# Revit family: TESK_Насос вертикальный_TK32-150
name_source: partatom
category: Оборудование
units: mm (PartAtom-declared; Revit-internal decimal feet)

## family parameters
Всегда вертикально = Да
Классификация = Насос
На основе рабочей плоскости = Нет
Общий = Нет
При загрузке вырезать с полостями = Нет
Размер круглого соединителя = Использовать диаметр
Тип детали = Вставляется
Точка расчета площади = Нет

## types (85) — shared parameters
ADSK_URL документации изделия = https://teskpump.ru
ADSK_Единица измерения = шт.
ADSK_Завод-изготовитель = TESK
ADSK_Классификация нагрузок = Прочее
ADSK_Количество = 1
ADSK_Коэффициент мощности = 1
URL = https://teskpump.ru
Изготовитель = TESK
Материал_1 = TESK_Черный_Условный
Материал_2 = TESK_Черный_Ребра_Условный
Плита_Толщина = 35 мм
Энергоэффективность = IE3

## per-type parameters (varying)
- ТК 32-18/2  1,1kW 3x380V 50Hz IE3: ADSK_Диаметр условный=32 мм; ADSK_Код изделия=55TK3218203380; ADSK_Количество фаз=3; ADSK_Количество фаз числовое=3; ADSK_Марка=ТК 32-18/2  1,1kW 3x380V 50Hz IE3; ADSK_Масса=36; ADSK_Масса_Текст=36; ADSK_Наименование=Вертикальный насос TESK типа IN-LINE, DN32, Hmax=18м (3x380V 50Hz IE3); ADSK_Напряжение=400 В; ADSK_Номинальная мощность=1.10 кВт; ADSK_Полная мощность=1.10 кВ·А; B1=170 мм; B2=142 мм; B3=125 мм; B4=117 мм; B5=144 мм; C=39 мм; D=120 мм; D2=80 мм; D3=134 мм; DN=32 мм; F0=140 мм; F1=78 мм; F2=39 мм; F3=88 мм; F4=104 мм; H1=100 мм; H2=189 мм; H3=540 мм; H4=251 мм; L1=340 мм; Напор максимальный=18; Плита_Глубина=188 мм; Плита_Ширина=188 мм
- ТК 32-21/2  1,5kW 3x380V 50Hz IE3: ADSK_Диаметр условный=32 мм; ADSK_Код изделия=55TK3221203380; ADSK_Количество фаз=3; ADSK_Количество фаз числовое=3; ADSK_Марка=ТК 32-21/2  1,5kW 3x380V 50Hz IE3; ADSK_Масса=40; ADSK_Масса_Текст=40; ADSK_Наименование=Вертикальный насос TESK типа IN-LINE, DN32, Hmax=21м (3x380V 50Hz IE3); ADSK_Напряжение=400 В; ADSK_Номинальная мощность=1.50 кВт; ADSK_Полная мощность=1.50 кВ·А; B1=190 мм; B2=155 мм; B3=125 мм; B4=117 мм; B5=144 мм; C=39 мм; D=140 мм; D2=100 мм; D3=134 мм; DN=32 мм; F0=140 мм; F1=78 мм; F2=39 мм; F3=88 мм; F4=104 мм; H1=100 мм; H2=199 мм; H3=592 мм; H4=293 мм; L1=340 мм; Напор максимальный=21; Плита_Глубина=188 мм; Плита_Ширина=188 мм
- ТК 32-25/2  2,2kW 3x380V 50Hz IE3: ADSK_Диаметр условный=32 мм; ADSK_Код изделия=55TK3225203380; ADSK_Количество фаз=3; ADSK_Количество фаз числовое=3; ADSK_Марка=ТК 32-25/2  2,2kW 3x380V 50Hz IE3; ADSK_Масса=42; ADSK_Масса_Текст=42; ADSK_Наименование=Вертикальный насос TESK типа IN-LINE, DN32, Hmax=25м (3x380V 50Hz IE3); ADSK_Напряжение=400 В; ADSK_Номинальная мощность=2.20 кВт; ADSK_Полная мощность=2.20 кВ·А; B1=190 мм; B2=155 мм; B3=125 мм; B4=117 мм; B5=144 мм; C=39 мм; D=140 мм; D2=100 мм; D3=134 мм; DN=32 мм; F0=140 мм; F1=78 мм; F2=39 мм; F3=88 мм; F4=104 мм; H1=100 мм; H2=199 мм; H3=592 мм; H4=293 мм; L1=340 мм; Напор максимальный=25; Плита_Глубина=188 мм; Плита_Ширина=188 мм
- ТК 32-18/2  1,1kW 1x220V 50Hz IE3: ADSK_Диаметр условный=32 мм; ADSK_Код изделия=55TK3218201220; ADSK_Количество фаз=1; ADSK_Количество фаз числовое=1; ADSK_Марка=ТК32-18/2  1,1kW 1x220V 50Hz IE3; ADSK_Масса=36; ADSK_Масса_Текст=36; ADSK_Наименование=Вертикальный насос TESK типа IN-LINE, DN32, Hmax=18м (1x220V 50Hz IE3); ADSK_Напряжение=230 В; ADSK_Номинальная мощность=1.10 кВт; ADSK_Полная мощность=1.10 кВ·А; B1=170 мм; B2=142 мм; B3=125 мм; B4=117 мм; B5=144 мм; C=39 мм; D=120 мм; D2=80 мм; D3=134 мм; DN=32 мм; F0=140 мм; F1=78 мм; F2=39 мм; F3=88 мм; F4=104 мм; H1=100 мм; H2=189 мм; H3=540 мм; H4=251 мм; L1=340 мм; Напор максимальный=18; Плита_Глубина=188 мм; Плита_Ширина=188 мм
- ТК 32-21/2  1,5kW 1x220V 50Hz IE3: ADSK_Диаметр условный=32 мм; ADSK_Код изделия=55TK3221201220; ADSK_Количество фаз=1; ADSK_Количество фаз числовое=1; ADSK_Марка=ТК32-21/2  1,5kW 1x220V 50Hz IE3; ADSK_Масса=40; ADSK_Масса_Текст=40; ADSK_Наименование=Вертикальный насос TESK типа IN-LINE, DN32, Hmax=21м (1x220V 50Hz IE3); ADSK_Напряжение=230 В; ADSK_Номинальная мощность=1.50 кВт; ADSK_Полная мощность=1.50 кВ·А; B1=190 мм; B2=155 мм; B3=125 мм; B4=117 мм; B5=144 мм; C=39 мм; D=140 мм; D2=100 мм; D3=134 мм; DN=32 мм; F0=140 мм; F1=78 мм; F2=39 мм; F3=88 мм; F4=104 мм; H1=100 мм; H2=199 мм; H3=592 мм; H4=293 мм; L1=340 мм; Напор максимальный=21; Плита_Глубина=188 мм; Плита_Ширина=188 мм
- ТК 32-25/2  2,2kW 1x220V 50Hz IE3: ADSK_Диаметр условный=32 мм; ADSK_Код изделия=55TK3225201220; ADSK_Количество фаз=1; ADSK_Количество фаз числовое=1; ADSK_Марка=ТК32-25/2  2,2kW 1x220V 50Hz IE3; ADSK_Масса=42; ADSK_Масса_Текст=42; ADSK_Наименование=Вертикальный насос TESK типа IN-LINE, DN32, Hmax=25м (1x220V 50Hz IE3); ADSK_Напряжение=230 В; ADSK_Номинальная мощность=2.20 кВт; ADSK_Полная мощность=2.20 кВ·А; B1=190 мм; B2=155 мм; B3=125 мм; B4=117 мм; B5=144 мм; C=39 мм; D=140 мм; D2=100 мм; D3=134 мм; DN=32 мм; F0=140 мм; F1=78 мм; F2=39 мм; F3=88 мм; F4=104 мм; H1=100 мм; H2=199 мм; H3=592 мм; H4=293 мм; L1=340 мм; Напор максимальный=25; Плита_Глубина=188 мм; Плита_Ширина=188 мм
- ТК 32-32/2  3kW 3x380V 50Hz IE3: ADSK_Диаметр условный=32 мм; ADSK_Код изделия=55TK3232203380; ADSK_Количество фаз=3; ADSK_Количество фаз числовое=3; ADSK_Марка=ТК 32-32/2  3kW 3x380V 50Hz IE3; ADSK_Масса=48; ADSK_Масса_Текст=48; ADSK_Наименование=Вертикальный насос TESK типа IN-LINE, DN32, Hmax=32м (3x380V 50Hz IE3); ADSK_Напряжение=400 В; ADSK_Номинальная мощность=3.00 кВт; ADSK_Полная мощность=3.00 кВ·А; B1=197 мм; B2=165 мм; B3=125 мм; B4=117 мм; B5=144 мм; C=39 мм; D=160 мм; D2=120 мм; D3=134 мм; DN=32 мм; F0=140 мм; F1=78 мм; F2=39 мм; F3=88 мм; F4=104 мм; H1=100 мм; H2=205 мм; H3=619 мм; H4=314 мм; L1=340 мм; Напор максимальный=32; Плита_Глубина=188 мм; Плита_Ширина=188 мм
- ТК 32-38/2  4kW 3x380V 50Hz IE3: ADSK_Диаметр условный=32 мм; ADSK_Код изделия=55TK3238203380; ADSK_Количество фаз=3; ADSK_Количество фаз числовое=3; ADSK_Марка=ТК 32-38/2  4kW 3x380V 50Hz IE3; ADSK_Масса=64; ADSK_Масса_Текст=64; ADSK_Наименование=Вертикальный насос TESK типа IN-LINE, DN32, Hmax=38м (3x380V 50Hz IE3); ADSK_Напряжение=400 В; ADSK_Номинальная мощность=4.00 кВт; ADSK_Полная мощность=4.00 кВ·А; B1=230 мм; B2=188 мм; B3=144 мм; B4=144 мм; B5=144 мм; C=39 мм; D=160 мм; D2=120 мм; D3=188 мм; DN=32 мм; F0=140 мм; F1=78 мм; F2=39 мм; F3=88 мм; F4=104 мм; H1=100 мм; H2=207 мм; H3=642 мм; H4=335 мм; L1=440 мм; Напор максимальный=38; Плита_Глубина=188 мм; Плита_Ширина=188 мм
- ТК 32-50/2  5,5kW 3x380V 50Hz IE3: ADSK_Диаметр условный=32 мм; ADSK_Код изделия=55TK3250203380; ADSK_Количество фаз=3; ADSK_Количество фаз числовое=3; ADSK_Марка=ТК 32-50/2  5,5kW 3x380V 50Hz IE3; ADSK_Масса=85; ADSK_Масса_Текст=85; ADSK_Наименование=Вертикальный насос TESK типа IN-LINE, DN32, Hmax=50м (3x380V 50Hz IE3); ADSK_Напряжение=400 В; ADSK_Номинальная мощность=5.50 кВт; ADSK_Полная мощность=5.50 кВ·А; B1=260 мм; B2=208 мм; B3=144 мм; B4=144 мм; B5=144 мм; C=39 мм; D=200 мм; D2=160 мм; D3=188 мм; DN=32 мм; F0=140 мм; F1=78 мм; F2=39 мм; F3=88 мм; F4=104 мм; H1=100 мм; H2=227 мм; H3=737 мм; H4=410 мм; L1=440 мм; Напор максимальный=50; Плита_Глубина=188 мм; Плита_Ширина=188 мм
- ТК 40-16/2  1,1kW 3x380V 50Hz IE3: ADSK_Диаметр условный=40 мм; ADSK_Код изделия=55TK4016203380; ADSK_Количество фаз=3; ADSK_Количество фаз числовое=3; ADSK_Марка=ТК 40-16/2  1,1kW 3x380V 50Hz IE3; ADSK_Масса=31; ADSK_Масса_Текст=31; ADSK_Наименование=Вертикальный насос TESK типа IN-LINE, DN40, Hmax=16м (3x380V 50Hz IE3); ADSK_Напряжение=400 В; ADSK_Номинальная мощность=1.10 кВт; ADSK_Полная мощность=1.10 кВ·А; B1=170 мм; B2=142 мм; B3=97 мм; B4=96 мм; B5=120 мм; C=44 мм; D=120 мм; D2=80 мм; D3=92 мм; DN=40 мм; F0=150 мм; F1=88 мм; F2=44 мм; F3=94 мм; F4=111 мм; H1=68 мм; H2=178 мм; H3=497 мм; H4=251 мм; L1=320 мм; Напор максимальный=16; Плита_Глубина=164 мм; Плита_Ширина=164 мм
- ТК 40-18/2  1,5kW 3x380V 50Hz IE3: ADSK_Диаметр условный=40 мм; ADSK_Код изделия=55TK4020203380; ADSK_Количество фаз=3; ADSK_Количество фаз числовое=3; ADSK_Марка=ТК 40-18/2  1,5kW 3x380V 50Hz IE3; ADSK_Масса=36; ADSK_Масса_Текст=36; ADSK_Наименование=Вертикальный насос TESK типа IN-LINE, DN40, Hmax=20м (3x380V 50Hz IE3); ADSK_Напряжение=400 В; ADSK_Номинальная мощность=1.50 кВт; ADSK_Полная мощность=1.50 кВ·А; B1=190 мм; B2=155 мм; B3=97 мм; B4=96 мм; B5=120 мм; C=44 мм; D=140 мм; D2=100 мм; D3=92 мм; DN=40 мм; F0=150 мм; F1=88 мм; F2=44 мм; F3=94 мм; F4=111 мм; H1=68 мм; H2=188 мм; H3=549 мм; H4=293 мм; L1=320 мм; Напор максимальный=20; Плита_Глубина=164 мм; Плита_Ширина=164 мм
- ТК 40-20/2  2,2kW 3x380V 50Hz IE3: ADSK_Диаметр условный=40 мм; ADSK_Код изделия=55TK4018203380; ADSK_Количество фаз=3; ADSK_Количество фаз числовое=3; ADSK_Марка=ТК 40-20/2  2,2kW 3x380V 50Hz IE3; ADSK_Масса=40; ADSK_Масса_Текст=40; ADSK_Наименование=Вертикальный насос TESK типа IN-LINE, DN40, Hmax=18м (3x380V 50Hz IE3); ADSK_Напряжение=400 В; ADSK_Номинальная мощность=2.20 кВт; ADSK_Полная мощность=2.20 кВ·А; B1=190 мм; B2=155 мм; B3=110 мм; B4=95 мм; B5=144 мм; C=44 мм; D=140 мм; D2=100 мм; D3=90 мм; DN=40 мм; F0=150 мм; F1=88 мм; F2=44 мм; F3=94 мм; F4=111 мм; H1=100 мм; H2=195 мм; H3=588 мм; H4=293 мм; L1=340 мм; Напор максимальный=18; Плита_Глубина=188 мм; Плита_Ширина=188 мм
- ТК 40-16/2  1,1kW 1x220V 50Hz IE3: ADSK_Диаметр условный=40 мм; ADSK_Код изделия=55TK4016201220; ADSK_Количество фаз=1; ADSK_Количество фаз числовое=1; ADSK_Марка=ТК 40-16/2  1,1kW 1x220V 50Hz IE3; ADSK_Масса=31; ADSK_Масса_Текст=31; ADSK_Наименование=Вертикальный насос TESK типа IN-LINE, DN40, Hmax=16м (1x220V 50Hz IE3); ADSK_Напряжение=230 В; ADSK_Номинальная мощность=1.10 кВт; ADSK_Полная мощность=1.10 кВ·А; B1=170 мм; B2=142 мм; B3=97 мм; B4=96 мм; B5=120 мм; C=44 мм; D=120 мм; D2=80 мм; D3=92 мм; DN=40 мм; F0=150 мм; F1=88 мм; F2=44 мм; F3=94 мм; F4=111 мм; H1=68 мм; H2=178 мм; H3=497 мм; H4=251 мм; L1=320 мм; Напор максимальный=16; Плита_Глубина=164 мм; Плита_Ширина=164 мм
- ТК 40-20/2  1,5kW 1x220V 50Hz IE3: ADSK_Диаметр условный=40 мм; ADSK_Код изделия=55TK4020201220; ADSK_Количество фаз=1; ADSK_Количество фаз числовое=1; ADSK_Марка=ТК 40-20/2  1,5kW 1x220V 50Hz IE3; ADSK_Масса=36; ADSK_Масса_Текст=36; ADSK_Наименование=Вертикальный насос TESK типа IN-LINE, DN40, Hmax=20м (1x220V 50Hz IE3); ADSK_Напряжение=230 В; ADSK_Номинальная мощность=1.50 кВт; ADSK_Полная мощность=1.50 кВ·А; B1=190 мм; B2=155 мм; B3=97 мм; B4=96 мм; B5=120 мм; C=44 мм; D=140 мм; D2=100 мм; D3=92 мм; DN=40 мм; F0=150 мм; F1=88 мм; F2=44 мм; F3=94 мм; F4=111 мм; H1=68 мм; H2=188 мм; H3=549 мм; H4=293 мм; L1=320 мм; Напор максимальный=20; Плита_Глубина=164 мм; Плита_Ширина=164 мм
- ТК 40-18/2  2,2kW 1x220V 50Hz IE3: ADSK_Диаметр условный=40 мм; ADSK_Код изделия=55TK4018201220; ADSK_Количество фаз=1; ADSK_Количество фаз числовое=1; ADSK_Марка=ТК 40-18/2  2,2kW 1x220V 50Hz IE3; ADSK_Масса=40; ADSK_Масса_Текст=40; ADSK_Наименование=Вертикальный насос TESK типа IN-LINE, DN40, Hmax=18м (1x220V 50Hz IE3); ADSK_Напряжение=230 В; ADSK_Номинальная мощность=2.20 кВт; ADSK_Полная мощность=2.20 кВ·А; B1=190 мм; B2=155 мм; B3=110 мм; B4=95 мм; B5=144 мм; C=44 мм; D=140 мм; D2=100 мм; D3=90 мм; DN=40 мм; F0=150 мм; F1=88 мм; F2=44 мм; F3=94 мм; F4=111 мм; H1=100 мм; H2=195 мм; H3=588 мм; H4=293 мм; L1=340 мм; Напор максимальный=18; Плита_Глубина=188 мм; Плита_Ширина=188 мм
- ТК 40-25/2  3kW 3x380V 50Hz IE3: ADSK_Диаметр условный=40 мм; ADSK_Код изделия=55TK4025203380; ADSK_Количество фаз=3; ADSK_Количество фаз числовое=3; ADSK_Марка=ТК 40-25/2  3kW 3x380V 50Hz IE3; ADSK_Масса=52; ADSK_Масса_Текст=52; ADSK_Наименование=Вертикальный насос TESK типа IN-LINE, DN40, Hmax=25м (3x380V 50Hz IE3); ADSK_Напряжение=400 В; ADSK_Номинальная мощность=3.00 кВт; ADSK_Полная мощность=3.00 кВ·А; B1=197 мм; B2=165 мм; B3=127 мм; B4=115 мм; B5=144 мм; C=44 мм; D=160 мм; D2=120 мм; D3=130 мм; DN=40 мм; F0=150 мм; F1=88 мм; F2=44 мм; F3=94 мм; F4=111 мм; H1=100 мм; H2=207 мм; H3=621 мм; H4=314 мм; L1=340 мм; Напор максимальный=25; Плита_Глубина=188 мм; Плита_Ширина=188 мм
- ТК 40-30/2  4kW 3x380V 50Hz IE3: ADSK_Диаметр условный=40 мм; ADSK_Код изделия=55TK4030203380; ADSK_Количество фаз=3; ADSK_Количество фаз числовое=3; ADSK_Марка=ТК 40-30/2  4kW 3x380V 50Hz IE3; ADSK_Масса=62; ADSK_Масса_Текст=62; ADSK_Наименование=Вертикальный насос TESK типа IN-LINE, DN40, Hmax=30м (3x380V 50Hz IE3); ADSK_Напряжение=400 В; ADSK_Номинальная мощность=4.00 кВт; ADSK_Полная мощность=4.00 кВ·А; B1=230 мм; B2=188 мм; B3=127 мм; B4=115 мм; B5=144 мм; C=44 мм; D=160 мм; D2=120 мм; D3=130 мм; DN=40 мм; F0=150 мм; F1=88 мм; F2=44 мм; F3=94 мм; F4=111 мм; H1=100 мм; H2=207 мм; H3=642 мм; H4=335 мм; L1=340 мм; Напор максимальный=30; Плита_Глубина=188 мм; Плита_Ширина=188 мм
- ТК 40-36/2  5,5kW 3x380V 50Hz IE3: ADSK_Диаметр условный=40 мм; ADSK_Код изделия=55TK4036203380; ADSK_Количество фаз=3; ADSK_Количество фаз числовое=3; ADSK_Марка=ТК 40-36/2  5,5kW 3x380V 50Hz IE3; ADSK_Масса=86; ADSK_Масса_Текст=86; ADSK_Наименование=Вертикальный насос TESK типа IN-LINE, DN40, Hmax=36м (3x380V 50Hz IE3); ADSK_Напряжение=400 В; ADSK_Номинальная мощность=5.50 кВт; ADSK_Полная мощность=5.50 кВ·А; B1=260 мм; B2=208 мм; B3=138 мм; B4=125 мм; B5=144 мм; C=44 мм; D=200 мм; D2=160 мм; D3=150 мм; DN=40 мм; F0=150 мм; F1=88 мм; F2=44 мм; F3=94 мм; F4=111 мм; H1=110 мм; H2=227 мм; H3=747 мм; H4=410 мм; L1=440 мм; Напор максимальный=36; Плита_Глубина=188 мм; Плита_Ширина=188 мм
- ТК 40-48/2  7,5kW 3x380V 50Hz IE3: ADSK_Диаметр условный=40 мм; ADSK_Код изделия=55TK4048203380; ADSK_Количество фаз=3; ADSK_Количество фаз числовое=3; ADSK_Марка=ТК 40-48/2  7,5kW 3x380V 50Hz IE3; ADSK_Масса=95; ADSK_Масса_Текст=95; ADSK_Наименование=Вертикальный насос TESK типа IN-LINE, DN40, Hmax=48м (3x380V 50Hz IE3); ADSK_Напряжение=400 В; ADSK_Номинальная мощность=7.50 кВт; ADSK_Полная мощность=7.50 кВ·А; B1=260 мм; B2=208 мм; B3=138 мм; B4=125 мм; B5=144 мм; C=44 мм; D=200 мм; D2=160 мм; D3=150 мм; DN=40 мм; F0=150 мм; F1=88 мм; F2=44 мм; F3=94 мм; F4=111 мм; H1=110 мм; H2=227 мм; H3=747 мм; H4=410 мм; L1=440 мм; Напор максимальный=48; Плита_Глубина=188 мм; Плита_Ширина=188 мм
- ТК 50-32/2  3kW 3x380V 50Hz IE3: ADSK_Диаметр условный=50 мм; ADSK_Код изделия=55TK5032203380; ADSK_Количество фаз=3; ADSK_Количество фаз числовое=3; ADSK_Марка=ТК 50-32/2  3kW 3x380V 50Hz IE3; ADSK_Масса=58; ADSK_Масса_Текст=58; ADSK_Наименование=Вертикальный насос TESK типа IN-LINE, DN50, Hmax=32м (3x380V 50Hz IE3); ADSK_Напряжение=400 В; ADSK_Номинальная мощность=3.00 кВт; ADSK_Полная мощность=3.00 кВ·А; B1=197 мм; B2=165 мм; B3=128 мм; B4=128 мм; B5=144 мм; C=51 мм; D=160 мм; D2=120 мм; D3=156 мм; DN=50 мм; F0=165 мм; F1=102 мм; F2=51 мм; F3=103 мм; F4=122 мм; H1=105 мм; H2=181 мм; H3=600 мм; H4=314 мм; L1=400 мм; Напор максимальный=32; Плита_Глубина=188 мм; Плита_Ширина=188 мм
- ТК 50-38/2  4kW 3x380V 50Hz IE3: ADSK_Диаметр условный=50 мм; ADSK_Код изделия=55TK5038203380; ADSK_Количество фаз=3; ADSK_Количество фаз числовое=3; ADSK_Марка=ТК 50-38/2  4kW 3x380V 50Hz IE3; ADSK_Масса=68; ADSK_Масса_Текст=68; ADSK_Наименование=Вертикальный насос TESK типа IN-LINE, DN50, Hmax=38м (3x380V 50Hz IE3); ADSK_Напряжение=400 В; ADSK_Номинальная мощность=4.00 кВт; ADSK_Полная мощность=4.00 кВ·А; B1=230 мм; B2=188 мм; B3=128 мм; B4=128 мм; B5=144 мм; C=51 мм; D=160 мм; D2=120 мм; D3=156 мм; DN=50 мм; F0=165 мм; F1=102 мм; F2=51 мм; F3=103 мм; F4=122 мм; H1=105 мм; H2=181 мм; H3=621 мм; H4=335 мм; L1=400 мм; Напор максимальный=38; Плита_Глубина=188 мм; Плита_Ширина=188 мм
- ТК 50-48/2  5,5kW 3x380V 50Hz IE3: ADSK_Диаметр условный=50 мм; ADSK_Код изделия=55TK5048203380; ADSK_Количество фаз=3; ADSK_Количество фаз числовое=3; ADSK_Марка=ТК 50-48/2  5,5kW 3x380V 50Hz IE3; ADSK_Масса=85; ADSK_Масса_Текст=85; ADSK_Наименование=Вертикальный насос TESK типа IN-LINE, DN50, Hmax=48м (3x380V 50Hz IE3); ADSK_Напряжение=400 В; ADSK_Номинальная мощность=5.50 кВт; ADSK_Полная мощность=5.50 кВ·А; B1=260 мм; B2=208 мм; B3=128 мм; B4=128 мм; B5=144 мм; C=51 мм; D=200 мм; D2=160 мм; D3=156 мм; DN=50 мм; F0=165 мм; F1=102 мм; F2=51 мм; F3=103 мм; F4=122 мм; H1=105 мм; H2=201 мм; H3=716 мм; H4=410 мм; L1=400 мм; Напор максимальный=48; Плита_Глубина=188 мм; Плита_Ширина=188 мм
- ТК 50-12/2  1,1kW 3x380V 50Hz IE3: ADSK_Диаметр условный=50 мм; ADSK_Код изделия=55TK5012203380; ADSK_Количество фаз=3; ADSK_Количество фаз числовое=3; ADSK_Марка=ТК 50-12/2  1,1kW 3x380V 50Hz IE3; ADSK_Масса=36; ADSK_Масса_Текст=36; ADSK_Наименование=Вертикальный насос TESK типа IN-LINE, DN50, Hmax=12м (3x380V 50Hz IE3); ADSK_Напряжение=400 В; ADSK_Номинальная мощность=1.10 кВт; ADSK_Полная мощность=1.10 кВ·А; B1=170 мм; B2=142 мм; B3=117 мм; B4=115 мм; B5=144 мм; C=51 мм; D=120 мм; D2=80 мм; D3=130 мм; DN=50 мм; F0=165 мм; F1=102 мм; F2=51 мм; F3=103 мм; F4=122 мм; H1=105 мм; H2=174 мм; H3=530 мм; H4=251 мм; L1=340 мм; Напор максимальный=12; Плита_Глубина=188 мм; Плита_Ширина=188 мм
- ТК 50-15/2  1,5kW 3x380V 50Hz IE3: ADSK_Диаметр условный=50 мм; ADSK_Код изделия=55TK5015203380; ADSK_Количество фаз=3; ADSK_Количество фаз числовое=3; ADSK_Марка=ТК 50-15/2  1,5kW 3x380V 50Hz IE3; ADSK_Масса=42; ADSK_Масса_Текст=42; ADSK_Наименование=Вертикальный насос TESK типа IN-LINE, DN50, Hmax=15м (3x380V 50Hz IE3); ADSK_Напряжение=400 В; ADSK_Номинальная мощность=1.50 кВт; ADSK_Полная мощность=1.50 кВ·А; B1=190 мм; B2=155 мм; B3=117 мм; B4=115 мм; B5=144 мм; C=51 мм; D=140 мм; D2=100 мм; D3=130 мм; DN=50 мм; F0=165 мм; F1=102 мм; F2=51 мм; F3=103 мм; F4=122 мм; H1=105 мм; H2=174 мм; H3=572 мм; H4=293 мм; L1=340 мм; Напор максимальный=15; Плита_Глубина=188 мм; Плита_Ширина=188 мм
- ТК 50-18/2  2,2kW 3x380V 50Hz IE3: ADSK_Диаметр условный=50 мм; ADSK_Код изделия=55TK5018203380; ADSK_Количество фаз=3; ADSK_Количество фаз числовое=3; ADSK_Марка=ТК 50-18/2  2,2kW 3x380V 50Hz IE3; ADSK_Масса=44; ADSK_Масса_Текст=44; ADSK_Наименование=Вертикальный насос TESK типа IN-LINE, DN50, Hmax=18м (3x380V 50Hz IE3); ADSK_Напряжение=400 В; ADSK_Номинальная мощность=2.20 кВт; ADSK_Полная мощность=2.20 кВ·А; B1=190 мм; B2=155 мм; B3=117 мм; B4=115 мм; B5=144 мм; C=51 мм; D=140 мм; D2=100 мм; D3=130 мм; DN=50 мм; F0=165 мм; F1=102 мм; F2=51 мм; F3=103 мм; F4=122 мм; H1=105 мм; H2=174 мм; H3=572 мм; H4=293 мм; L1=340 мм; Напор максимальный=18; Плита_Глубина=188 мм; Плита_Ширина=188 мм
- ТК 50-12/2  1,1kW 3x220V 50Hz IE3: ADSK_Диаметр условный=50 мм; ADSK_Код изделия=55TK5012201220; ADSK_Количество фаз=3; ADSK_Количество фаз числовое=3; ADSK_Марка=ТК 50-12/2  1,1kW 3x220V 50Hz IE3; ADSK_Масса=36; ADSK_Масса_Текст=36; ADSK_Наименование=Вертикальный насос TESK типа IN-LINE, DN50, Hmax=12м (3x380V 50Hz IE3); ADSK_Напряжение=400 В; ADSK_Номинальная мощность=1.10 кВт; ADSK_Полная мощность=1.10 кВ·А; B1=170 мм; B2=142 мм; B3=117 мм; B4=115 мм; B5=144 мм; C=51 мм; D=120 мм; D2=80 мм; D3=130 мм; DN=50 мм; F0=165 мм; F1=102 мм; F2=51 мм; F3=103 мм; F4=122 мм; H1=105 мм; H2=174 мм; H3=530 мм; H4=251 мм; L1=340 мм; Напор максимальный=12; Плита_Глубина=188 мм; Плита_Ширина=188 мм
- ТК 50-15/2  1,5kW 3x220V 50Hz IE3: ADSK_Диаметр условный=50 мм; ADSK_Код изделия=55TK5015201220; ADSK_Количество фаз=3; ADSK_Количество фаз числовое=3; ADSK_Марка=ТК 50-15/2  1,5kW 3x220V 50Hz IE3; ADSK_Масса=42; ADSK_Масса_Текст=42; ADSK_Наименование=Вертикальный насос TESK типа IN-LINE, DN50, Hmax=15м (3x380V 50Hz IE3); ADSK_Напряжение=400 В; ADSK_Номинальная мощность=1.50 кВт; ADSK_Полная мощность=1.50 кВ·А; B1=190 мм; B2=155 мм; B3=117 мм; B4=115 мм; B5=144 мм; C=51 мм; D=140 мм; D2=100 мм; D3=130 мм; DN=50 мм; F0=165 мм; F1=102 мм; F2=51 мм; F3=103 мм; F4=122 мм; H1=105 мм; H2=174 мм; H3=572 мм; H4=293 мм; L1=340 мм; Напор максимальный=15; Плита_Глубина=188 мм; Плита_Ширина=188 мм
- ТК 50-18/2  2,2kW 3x220V 50Hz IE3: ADSK_Диаметр условный=50 мм; ADSK_Код изделия=55TK5018201220; ADSK_Количество фаз=3; ADSK_Количество фаз числовое=3; ADSK_Марка=ТК 50-18/2  2,2kW 3x220V 50Hz IE3; ADSK_Масса=44; ADSK_Масса_Текст=44; ADSK_Наименование=Вертикальный насос TESK типа IN-LINE, DN50, Hmax=18м (3x380V 50Hz IE3); ADSK_Напряжение=400 В; ADSK_Номинальная мощность=2.20 кВт; ADSK_Полная мощность=2.20 кВ·А; B1=190 мм; B2=155 мм; B3=117 мм; B4=115 мм; B5=144 мм; C=51 мм; D=140 мм; D2=100 мм; D3=130 мм; DN=50 мм; F0=165 мм; F1=102 мм; F2=51 мм; F3=103 мм; F4=122 мм; H1=105 мм; H2=174 мм; H3=572 мм; H4=293 мм; L1=340 мм; Напор максимальный=18; Плита_Глубина=188 мм; Плита_Ширина=188 мм
- ТК 50-24/2  3kW 3x380V 50Hz IE3: ADSK_Диаметр условный=50 мм; ADSK_Код изделия=55TK5024203380; ADSK_Количество фаз=3; ADSK_Количество фаз числовое=3; ADSK_Марка=ТК 50-24/2  3kW 3x380V 50Hz IE3; ADSK_Масса=50; ADSK_Масса_Текст=50; ADSK_Наименование=Вертикальный насос TESK типа IN-LINE, DN50, Hmax=24м (3x380V 50Hz IE3); ADSK_Напряжение=400 В; ADSK_Номинальная мощность=3.00 кВт; ADSK_Полная мощность=3.00 кВ·А; B1=197 мм; B2=165 мм; B3=117 мм; B4=115 мм; B5=144 мм; C=51 мм; D=160 мм; D2=120 мм; D3=130 мм; DN=50 мм; F0=165 мм; F1=102 мм; F2=51 мм; F3=103 мм; F4=122 мм; H1=105 мм; H2=184 мм; H3=603 мм; H4=314 мм; L1=340 мм; Напор максимальный=24; Плита_Глубина=188 мм; Плита_Ширина=188 мм
- ТК 50-28/2  4kW 3x380V 50Hz IE3: ADSK_Диаметр условный=50 мм; ADSK_Код изделия=55TK5028203380; ADSK_Количество фаз=3; ADSK_Количество фаз числовое=3; ADSK_Марка=ТК 50-28/2  4kW 3x380V 50Hz IE3; ADSK_Масса=64; ADSK_Масса_Текст=64; ADSK_Наименование=Вертикальный насос TESK типа IN-LINE, DN50, Hmax=28м (3x380V 50Hz IE3); ADSK_Напряжение=400 В; ADSK_Номинальная мощность=4.00 кВт; ADSK_Полная мощность=4.00 кВ·А; B1=230 мм; B2=188 мм; B3=129 мм; B4=115 мм; B5=144 мм; C=51 мм; D=160 мм; D2=120 мм; D3=130 мм; DN=50 мм; F0=165 мм; F1=102 мм; F2=51 мм; F3=103 мм; F4=122 мм; H1=115 мм; H2=198 мм; H3=648 мм; H4=335 мм; L1=340 мм; Напор максимальный=28; Плита_Глубина=188 мм; Плита_Ширина=188 мм
- ТК 50-35/2  5,5kW 3x380V 50Hz IE3: ADSK_Диаметр условный=50 мм; ADSK_Код изделия=55TK5035203380; ADSK_Количество фаз=3; ADSK_Количество фаз числовое=3; ADSK_Марка=ТК 50-35/2  5,5kW 3x380V 50Hz IE3; ADSK_Масса=83; ADSK_Масса_Текст=83; ADSK_Наименование=Вертикальный насос TESK типа IN-LINE, DN50, Hmax=35м (3x380V 50Hz IE3); ADSK_Напряжение=400 В; ADSK_Номинальная мощность=5.50 кВт; ADSK_Полная мощность=5.50 кВ·А; B1=260 мм; B2=208 мм; B3=129 мм; B4=115 мм; B5=144 мм; C=51 мм; D=200 мм; D2=160 мм; D3=130 мм; DN=50 мм; F0=165 мм; F1=102 мм; F2=51 мм; F3=103 мм; F4=122 мм; H1=115 мм; H2=218 мм; H3=742 мм; H4=409 мм; L1=340 мм; Напор максимальный=35; Плита_Глубина=188 мм; Плита_Ширина=188 мм
- ТК 50-40/2  7,5kW 3x380V 50Hz IE3: ADSK_Диаметр условный=50 мм; ADSK_Код изделия=55TK5040203380; ADSK_Количество фаз=3; ADSK_Количество фаз числовое=3; ADSK_Марка=ТК 50-40/2  7,5kW 3x380V 50Hz IE3; ADSK_Масса=98; ADSK_Масса_Текст=98; ADSK_Наименование=Вертикальный насос TESK типа IN-LINE, DN50, Hmax=40м (3x380V 50Hz IE3); ADSK_Напряжение=400 В; ADSK_Номинальная мощность=7.50 кВт; ADSK_Полная мощность=7.50 кВ·А; B1=260 мм; B2=208 мм; B3=171 мм; B4=158 мм; B5=144 мм; C=51 мм; D=200 мм; D2=160 мм; D3=216 мм; DN=50 мм; F0=165 мм; F1=102 мм; F2=51 мм; F3=103 мм; F4=122 мм; H1=115 мм; H2=215 мм; H3=740 мм; H4=410 мм; L1=440 мм; Напор максимальный=40; Плита_Глубина=188 мм; Плита_Ширина=188 мм
- ТК 50-50/2  11kW 3x380V 50Hz IE3: ADSK_Диаметр условный=50 мм; ADSK_Код изделия=55TK5050203380; ADSK_Количество фаз=3; ADSK_Количество фаз числовое=3; ADSK_Марка=ТК 50-50/2  11kW 3x380V 50Hz IE3; ADSK_Масса=172; ADSK_Масса_Текст=172; ADSK_Наименование=Вертикальный насос TESK типа IN-LINE, DN50, Hmax=50м (3x380V 50Hz IE3); ADSK_Напряжение=400 В; ADSK_Номинальная мощность=11.00 кВт; ADSK_Полная мощность=11.00 кВ·А; B1=330 мм; B2=255 мм; B3=171 мм; B4=158 мм; B5=144 мм; C=51 мм; D=350 мм; D2=225 мм; D3=216 мм; DN=50 мм; F0=165 мм; F1=102 мм; F2=51 мм; F3=103 мм; F4=122 мм; H1=115 мм; H2=245 мм; H3=902 мм; H4=542 мм; L1=440 мм; Напор максимальный=50; Плита_Глубина=188 мм; Плита_Ширина=188 мм
- ТК 50-60/2  15kW 3x380V 50Hz IE3: ADSK_Диаметр условный=50 мм; ADSK_Код изделия=55TK5060203380; ADSK_Количество фаз=3; ADSK_Количество фаз числовое=3; ADSK_Марка=ТК 50-60/2  15kW 3x380V 50Hz IE3; ADSK_Масса=182; ADSK_Масса_Текст=182; ADSK_Наименование=Вертикальный насос TESK типа IN-LINE, DN50, Hmax=60м (3x380V 50Hz IE3); ADSK_Напряжение=400 В; ADSK_Номинальная мощность=15.00 кВт; ADSK_Полная мощность=15.00 кВ·А; B1=330 мм; B2=255 мм; B3=171 мм; B4=158 мм; B5=144 мм; C=51 мм; D=350 мм; D2=225 мм; D3=216 мм; DN=50 мм; F0=165 мм; F1=102 мм; F2=51 мм; F3=103 мм; F4=122 мм; H1=115 мм; H2=245 мм; H3=935 мм; H4=575 мм; L1=440 мм; Напор максимальный=60; Плита_Глубина=188 мм; Плита_Ширина=188 мм
- ТК 50-70/2  18,5kW 3x380V 50Hz IE3: ADSK_Диаметр условный=50 мм; ADSK_Код изделия=55TK5070203380; ADSK_Количество фаз=3; ADSK_Количество фаз числовое=3; ADSK_Марка=ТК 50-70/2  18,5kW 3x380V 50Hz IE3; ADSK_Масса=196; ADSK_Масса_Текст=196; ADSK_Наименование=Вертикальный насос TESK типа IN-LINE, DN50, Hmax=70м (3x380V 50Hz IE3); ADSK_Напряжение=400 В; ADSK_Номинальная мощность=18.50 кВт; ADSK_Полная мощность=18.50 кВ·А; B1=330 мм; B2=255 мм; B3=171 мм; B4=158 мм; B5=144 мм; C=51 мм; D=350 мм; D2=225 мм; D3=216 мм; DN=50 мм; F0=165 мм; F1=102 мм; F2=51 мм; F3=103 мм; F4=122 мм; H1=115 мм; H2=245 мм; H3=935 мм; H4=575 мм; L1=440 мм; Напор максимальный=70; Плита_Глубина=188 мм; Плита_Ширина=188 мм
- ТК 50-81/2  22kW 3x380V 50Hz IE3: ADSK_Диаметр условный=50 мм; ADSK_Код изделия=55TK5081203380; ADSK_Количество фаз=3; ADSK_Количество фаз числовое=3; ADSK_Марка=ТК 50-81/2  22kW 3x380V 50Hz IE3; ADSK_Масса=238; ADSK_Масса_Текст=238; ADSK_Наименование=Вертикальный насос TESK типа IN-LINE, DN50, Hmax=81м (3x380V 50Hz IE3); ADSK_Напряжение=400 В; ADSK_Номинальная мощность=22.00 кВт; ADSK_Полная мощность=22.00 кВ·А; B1=360 мм; B2=280 мм; B3=171 мм; B4=158 мм; B5=144 мм; C=51 мм; D=350 мм; D2=250 мм; D3=216 мм; DN=50 мм; F0=165 мм; F1=102 мм; F2=51 мм; F3=103 мм; F4=122 мм; H1=115 мм; H2=245 мм; H3=965 мм; H4=605 мм; L1=440 мм; Напор максимальный=81; Плита_Глубина=188 мм; Плита_Ширина=188 мм
- ТК 65-36/2  5,5kW 3x380V 50Hz IE3: ADSK_Диаметр условный=65 мм; ADSK_Код изделия=55TK6536203380; ADSK_Количество фаз=3; ADSK_Количество фаз числовое=3; ADSK_Марка=ТК 65-36/2  5,5kW 3x380V 50Hz IE3; ADSK_Масса=87; ADSK_Масса_Текст=87; ADSK_Наименование=Вертикальный насос TESK типа IN-LINE, DN65, Hmax=36м (3x380V 50Hz IE3); ADSK_Напряжение=400 В; ADSK_Номинальная мощность=5.50 кВт; ADSK_Полная мощность=5.50 кВ·А; B1=260 мм; B2=208 мм; B3=128 мм; B4=128 мм; B5=144 мм; C=61 мм; D=200 мм; D2=160 мм; D3=156 мм; DN=65 мм; F0=185 мм; F1=122 мм; F2=61 мм; F3=116 мм; F4=137 мм; H1=105 мм; H2=209 мм; H3=724 мм; H4=410 мм; L1=400 мм; Напор максимальный=36; Плита_Глубина=188 мм; Плита_Ширина=188 мм
- ТК 65-48/2  7,5kW 3x380V 50Hz IE3: ADSK_Диаметр условный=65 мм; ADSK_Код изделия=55TK6548203380; ADSK_Количество фаз=3; ADSK_Количество фаз числовое=3; ADSK_Марка=ТК 65-48/2  7,5kW 3x380V 50Hz IE3; ADSK_Масса=94; ADSK_Масса_Текст=94; ADSK_Наименование=Вертикальный насос TESK типа IN-LINE, DN65, Hmax=48м (3x380V 50Hz IE3); ADSK_Напряжение=400 В; ADSK_Номинальная мощность=7.50 кВт; ADSK_Полная мощность=7.50 кВ·А; B1=260 мм; B2=208 мм; B3=128 мм; B4=128 мм; B5=144 мм; C=61 мм; D=200 мм; D2=160 мм; D3=156 мм; DN=65 мм; F0=185 мм; F1=122 мм; F2=61 мм; F3=116 мм; F4=137 мм; H1=105 мм; H2=209 мм; H3=724 мм; H4=410 мм; L1=400 мм; Напор максимальный=48; Плита_Глубина=188 мм; Плита_Ширина=188 мм
- ТК 65-15/2  2,2kW 3x380V 50Hz IE3: ADSK_Диаметр условный=65 мм; ADSK_Код изделия=55TK6515203380; ADSK_Количество фаз=3; ADSK_Количество фаз числовое=3; ADSK_Марка=ТК 65-15/2  2,2kW 3x380V 50Hz IE3; ADSK_Масса=48; ADSK_Масса_Текст=48; ADSK_Наименование=Вертикальный насос TESK типа IN-LINE, DN65, Hmax=15м (3x380V 50Hz IE3); ADSK_Напряжение=400 В; ADSK_Номинальная мощность=2.20 кВт; ADSK_Полная мощность=2.20 кВ·А; B1=190 мм; B2=155 мм; B3=142 мм; B4=124 мм; B5=144 мм; C=61 мм; D=140 мм; D2=100 мм; D3=148 мм; DN=65 мм; F0=185 мм; F1=122 мм; F2=61 мм; F3=116 мм; F4=137 мм; H1=105 мм; H2=193 мм; H3=591 мм; H4=293 мм; L1=360 мм; Напор максимальный=15; Плита_Глубина=188 мм; Плита_Ширина=188 мм
- ТК 65-15/2  2,2kW 1x220V 50Hz IE3: ADSK_Диаметр условный=65 мм; ADSK_Код изделия=55TK6515201220; ADSK_Количество фаз=1; ADSK_Количество фаз числовое=1; ADSK_Марка=ТК 65-15/2  2,2kW 1x220V 50Hz IE3; ADSK_Масса=48; ADSK_Масса_Текст=48; ADSK_Наименование=Вертикальный насос TESK типа IN-LINE, DN65, Hmax=15м (1x220V 50Hz IE3); ADSK_Напряжение=230 В; ADSK_Номинальная мощность=2.20 кВт; ADSK_Полная мощность=2.20 кВ·А; B1=190 мм; B2=155 мм; B3=142 мм; B4=124 мм; B5=144 мм; C=61 мм; D=140 мм; D2=100 мм; D3=148 мм; DN=65 мм; F0=185 мм; F1=122 мм; F2=61 мм; F3=116 мм; F4=137 мм; H1=105 мм; H2=193 мм; H3=591 мм; H4=293 мм; L1=360 мм; Напор максимальный=15; Плита_Глубина=188 мм; Плита_Ширина=188 мм
- ТК 65-19/2  3kW 3x380V 50Hz IE3: ADSK_Диаметр условный=65 мм; ADSK_Код изделия=55TK6519203380; ADSK_Количество фаз=3; ADSK_Количество фаз числовое=3; ADSK_Марка=ТК 65-19/2  3kW 3x380V 50Hz IE3; ADSK_Масса=57; ADSK_Масса_Текст=57; ADSK_Наименование=Вертикальный насос TESK типа IN-LINE, DN65, Hmax=19м (3x380V 50Hz IE3); ADSK_Напряжение=400 В; ADSK_Номинальная мощность=3.00 кВт; ADSK_Полная мощность=3.00 кВ·А; B1=197 мм; B2=165 мм; B3=142 мм; B4=124 мм; B5=144 мм; C=61 мм; D=160 мм; D2=120 мм; D3=148 мм; DN=65 мм; F0=185 мм; F1=122 мм; F2=61 мм; F3=116 мм; F4=137 мм; H1=105 мм; H2=203 мм; H3=622 мм; H4=314 мм; L1=360 мм; Напор максимальный=19; Плита_Глубина=188 мм; Плита_Ширина=188 мм
- ТК 65-22/2  4kW 3x380V 50Hz IE3: ADSK_Диаметр условный=65 мм; ADSK_Код изделия=55TK6522203380; ADSK_Количество фаз=3; ADSK_Количество фаз числовое=3; ADSK_Марка=ТК 65-22/2  4kW 3x380V 50Hz IE3; ADSK_Масса=65; ADSK_Масса_Текст=65; ADSK_Наименование=Вертикальный насос TESK типа IN-LINE, DN65, Hmax=22м (3x380V 50Hz IE3); ADSK_Напряжение=400 В; ADSK_Номинальная мощность=4.00 кВт; ADSK_Полная мощность=4.00 кВ·А; B1=230 мм; B2=188 мм; B3=142 мм; B4=124 мм; B5=144 мм; C=61 мм; D=160 мм; D2=120 мм; D3=148 мм; DN=65 мм; F0=185 мм; F1=122 мм; F2=61 мм; F3=116 мм; F4=137 мм; H1=105 мм; H2=203 мм; H3=643 мм; H4=335 мм; L1=360 мм; Напор максимальный=22; Плита_Глубина=188 мм; Плита_Ширина=188 мм
- ТК 65-30/2  5,5kW 3x380V 50Hz IE3: ADSK_Диаметр условный=65 мм; ADSK_Код изделия=55TK6530203380; ADSK_Количество фаз=3; ADSK_Количество фаз числовое=3; ADSK_Марка=ТК 65-30/2  5,5kW 3x380V 50Hz IE3; ADSK_Масса=84; ADSK_Масса_Текст=84; ADSK_Наименование=Вертикальный насос TESK типа IN-LINE, DN65, Hmax=30м (3x380V 50Hz IE3); ADSK_Напряжение=400 В; ADSK_Номинальная мощность=5.50 кВт; ADSK_Полная мощность=5.50 кВ·А; B1=260 мм; B2=208 мм; B3=142 мм; B4=124 мм; B5=144 мм; C=61 мм; D=200 мм; D2=160 мм; D3=148 мм; DN=65 мм; F0=185 мм; F1=122 мм; F2=61 мм; F3=116 мм; F4=137 мм; H1=105 мм; H2=223 мм; H3=738 мм; H4=410 мм; L1=360 мм; Напор максимальный=30; Плита_Глубина=188 мм; Плита_Ширина=188 мм
- ТК 65-34/2  7,5kW 3x380V 50Hz IE3: ADSK_Диаметр условный=65 мм; ADSK_Код изделия=55TK6534203380; ADSK_Количество фаз=3; ADSK_Количество фаз числовое=3; ADSK_Марка=ТК 65-34/2  7,5kW 3x380V 50Hz IE3; ADSK_Масса=91; ADSK_Масса_Текст=91; ADSK_Наименование=Вертикальный насос TESK типа IN-LINE, DN65, Hmax=34м (3x380V 50Hz IE3); ADSK_Напряжение=400 В; ADSK_Номинальная мощность=7.50 кВт; ADSK_Полная мощность=7.50 кВ·А; B1=260 мм; B2=208 мм; B3=142 мм; B4=124 мм; B5=144 мм; C=61 мм; D=200 мм; D2=160 мм; D3=148 мм; DN=65 мм; F0=185 мм; F1=122 мм; F2=61 мм; F3=116 мм; F4=137 мм; H1=105 мм; H2=223 мм; H3=738 мм; H4=410 мм; L1=360 мм; Напор максимальный=34; Плита_Глубина=188 мм; Плита_Ширина=188 мм
- ТК 65-40/2  11kW 3x380V 50Hz IE3: ADSK_Диаметр условный=65 мм; ADSK_Код изделия=55TK6540203380; ADSK_Количество фаз=3; ADSK_Количество фаз числовое=3; ADSK_Марка=ТК 65-40/2  11kW 3x380V 50Hz IE3; ADSK_Масса=178; ADSK_Масса_Текст=178; ADSK_Наименование=Вертикальный насос TESK типа IN-LINE, DN65, Hmax=40м (3x380V 50Hz IE3); ADSK_Напряжение=400 В; ADSK_Номинальная мощность=11.00 кВт; ADSK_Полная мощность=11.00 кВ·А; B1=330 мм; B2=255 мм; B3=179 мм; B4=167 мм; B5=144 мм; C=61 мм; D=350 мм; D2=225 мм; D3=234 мм; DN=65 мм; F0=185 мм; F1=122 мм; F2=61 мм; F3=116 мм; F4=137 мм; H1=125 мм; H2=257 мм; H3=924 мм; H4=542 мм; L1=475 мм; Напор максимальный=40; Плита_Глубина=188 мм; Плита_Ширина=188 мм
- ТК 65-50/2  15kW 3x380V 50Hz IE3: ADSK_Диаметр условный=65 мм; ADSK_Код изделия=55TK6550203380; ADSK_Количество фаз=3; ADSK_Количество фаз числовое=3; ADSK_Марка=ТК 65-50/2  15kW 3x380V 50Hz IE3; ADSK_Масса=190; ADSK_Масса_Текст=190; ADSK_Наименование=Вертикальный насос TESK типа IN-LINE, DN65, Hmax=50м (3x380V 50Hz IE3); ADSK_Напряжение=400 В; ADSK_Номинальная мощность=15.00 кВт; ADSK_Полная мощность=15.00 кВ·А; B1=330 мм; B2=255 мм; B3=179 мм; B4=167 мм; B5=144 мм; C=61 мм; D=350 мм; D2=225 мм; D3=234 мм; DN=65 мм; F0=185 мм; F1=122 мм; F2=61 мм; F3=116 мм; F4=137 мм; H1=125 мм; H2=257 мм; H3=957 мм; H4=575 мм; L1=475 мм; Напор максимальный=50; Плита_Глубина=188 мм; Плита_Ширина=188 мм
- ТК 65-61/2  18,5kW 3x380V 50Hz IE3: ADSK_Диаметр условный=65 мм; ADSK_Код изделия=55TK6561203380; ADSK_Количество фаз=3; ADSK_Количество фаз числовое=3; ADSK_Марка=ТК 65-61/2  18,5kW 3x380V 50Hz IE3; ADSK_Масса=202; ADSK_Масса_Текст=202; ADSK_Наименование=Вертикальный насос TESK типа IN-LINE, DN65, Hmax=61м (3x380V 50Hz IE3); ADSK_Напряжение=400 В; ADSK_Номинальная мощность=18.50 кВт; ADSK_Полная мощность=18.50 кВ·А; B1=330 мм; B2=255 мм; B3=179 мм; B4=167 мм; B5=144 мм; C=61 мм; D=350 мм; D2=225 мм; D3=234 мм; DN=65 мм; F0=185 мм; F1=122 мм; F2=61 мм; F3=116 мм; F4=137 мм; H1=125 мм; H2=257 мм; H3=957 мм; H4=575 мм; L1=475 мм; Напор максимальный=61; Плита_Глубина=188 мм; Плита_Ширина=188 мм
- ТК 65-67/2  22kW 3x380V 50Hz IE3: ADSK_Диаметр условный=65 мм; ADSK_Код изделия=55TK6567203380; ADSK_Количество фаз=3; ADSK_Количество фаз числовое=3; ADSK_Марка=ТК 65-67/2  22kW 3x380V 50Hz IE3; ADSK_Масса=242; ADSK_Масса_Текст=242; ADSK_Наименование=Вертикальный насос TESK типа IN-LINE, DN65, Hmax=67м (3x380V 50Hz IE3); ADSK_Напряжение=400 В; ADSK_Номинальная мощность=22.00 кВт; ADSK_Полная мощность=22.00 кВ·А; B1=330 мм; B2=280 мм; B3=179 мм; B4=167 мм; B5=144 мм; C=61 мм; D=350 мм; D2=250 мм; D3=234 мм; DN=65 мм; F0=185 мм; F1=122 мм; F2=61 мм; F3=116 мм; F4=137 мм; H1=125 мм; H2=257 мм; H3=987 мм; H4=605 мм; L1=475 мм; Напор максимальный=67; Плита_Глубина=188 мм; Плита_Ширина=188 мм
- ТК 65-83/2  30kW 3x380V 50Hz IE3: ADSK_Диаметр условный=65 мм; ADSK_Код изделия=55TK6583203380; ADSK_Количество фаз=3; ADSK_Количество фаз числовое=3; ADSK_Марка=ТК 65-83/2  30kW 3x380V 50Hz IE3; ADSK_Масса=298; ADSK_Масса_Текст=298; ADSK_Наименование=Вертикальный насос TESK типа IN-LINE, DN65, Hmax=83м (3x380V 50Hz IE3); ADSK_Напряжение=400 В; ADSK_Номинальная мощность=30.00 кВт; ADSK_Полная мощность=30.00 кВ·А; B1=400 мм; B2=305 мм; B3=179 мм; B4=167 мм; B5=144 мм; C=61 мм; D=400 мм; D2=275 мм; D3=234 мм; DN=65 мм; F0=185 мм; F1=122 мм; F2=61 мм; F3=116 мм; F4=137 мм; H1=125 мм; H2=257 мм; H3=1047 мм; H4=665 мм; L1=475 мм; Напор максимальный=83; Плита_Глубина=188 мм; Плита_Ширина=188 мм
- ТК 80-40/2  11kW 3x380V 50Hz IE3: ADSK_Диаметр условный=80 мм; ADSK_Код изделия=55TK8040203380; ADSK_Количество фаз=3; ADSK_Количество фаз числовое=3; ADSK_Марка=ТК 80-40/2  11kW 3x380V 50Hz IE3; ADSK_Масса=172; ADSK_Масса_Текст=172; ADSK_Наименование=Вертикальный насос TESK типа IN-LINE, DN80, Hmax=40м (3x380V 50Hz IE3); ADSK_Напряжение=400 В; ADSK_Номинальная мощность=3.00 кВт; ADSK_Полная мощность=3.00 кВ·А; B1=330 мм; B2=255 мм; B3=137 мм; B4=128 мм; B5=144 мм; C=66 мм; D=350 мм; D2=225 мм; D3=156 мм; DN=80 мм; F0=200 мм; F1=132 мм; F2=66 мм; F3=125 мм; F4=148 мм; H1=115 мм; H2=235 мм; H3=892 мм; H4=542 мм; L1=500 мм; Напор максимальный=40; Плита_Глубина=188 мм; Плита_Ширина=188 мм
- ТК 80-48/2  15kW 3x380V 50Hz IE3: ADSK_Диаметр условный=80 мм; ADSK_Код изделия=55TK8048203380; ADSK_Количество фаз=3; ADSK_Количество фаз числовое=3; ADSK_Марка=ТК 80-48/2  15kW 3x380V 50Hz IE3; ADSK_Масса=183; ADSK_Масса_Текст=183; ADSK_Наименование=Вертикальный насос TESK типа IN-LINE, DN80, Hmax=48м (3x380V 50Hz IE3); ADSK_Напряжение=400 В; ADSK_Номинальная мощность=4.00 кВт; ADSK_Полная мощность=4.00 кВ·А; B1=330 мм; B2=255 мм; B3=137 мм; B4=128 мм; B5=144 мм; C=66 мм; D=350 мм; D2=225 мм; D3=156 мм; DN=80 мм; F0=200 мм; F1=132 мм; F2=66 мм; F3=125 мм; F4=148 мм; H1=115 мм; H2=235 мм; H3=925 мм; H4=575 мм; L1=500 мм; Напор максимальный=48; Плита_Глубина=188 мм; Плита_Ширина=188 мм
- ТК 80-13/2  3kW 3x380V 50Hz IE3: ADSK_Диаметр условный=80 мм; ADSK_Код изделия=55TK8013203380; ADSK_Количество фаз=3; ADSK_Количество фаз числовое=3; ADSK_Марка=ТК 80-13/2  3kW 3x380V 50Hz IE3; ADSK_Масса=64; ADSK_Масса_Текст=64; ADSK_Наименование=Вертикальный насос TESK типа IN-LINE, DN80, Hmax=13м (3x380V 50Hz IE3); ADSK_Напряжение=400 В; ADSK_Номинальная мощность=5.50 кВт; ADSK_Полная мощность=5.50 кВ·А; B1=197 мм; B2=165 мм; B3=142 мм; B4=124 мм; B5=160 мм; C=66 мм; D=160 мм; D2=120 мм; D3=148 мм; DN=80 мм; F0=200 мм; F1=132 мм; F2=66 мм; F3=125 мм; F4=148 мм; H1=97 мм; H2=243 мм; H3=654 мм; H4=314 мм; L1=450 мм; Напор максимальный=13; Плита_Глубина=204 мм; Плита_Ширина=204 мм
- ТК 80-18/2  4kW 3x380V 50Hz IE3: ADSK_Диаметр условный=80 мм; ADSK_Код изделия=55TK8018203380; ADSK_Количество фаз=3; ADSK_Количество фаз числовое=3; ADSK_Марка=ТК 80-18/2  4kW 3x380V 50Hz IE3; ADSK_Масса=72; ADSK_Масса_Текст=72; ADSK_Наименование=Вертикальный насос TESK типа IN-LINE, DN80, Hmax=18м (3x380V 50Hz IE3); ADSK_Напряжение=400 В; ADSK_Номинальная мощность=7.50 кВт; ADSK_Полная мощность=7.50 кВ·А; B1=230 мм; B2=188 мм; B3=142 мм; B4=124 мм; B5=160 мм; C=66 мм; D=160 мм; D2=120 мм; D3=148 мм; DN=80 мм; F0=200 мм; F1=132 мм; F2=66 мм; F3=125 мм; F4=148 мм; H1=97 мм; H2=243 мм; H3=675 мм; H4=335 мм; L1=450 мм; Напор максимальный=18; Плита_Глубина=204 мм; Плита_Ширина=204 мм
- ТК 80-22/2  5,5kW 3x380V 50Hz IE3: ADSK_Диаметр условный=80 мм; ADSK_Код изделия=55TK8022203380; ADSK_Количество фаз=3; ADSK_Количество фаз числовое=3; ADSK_Марка=ТК 80-22/2  5,5kW 3x380V 50Hz IE3; ADSK_Масса=90; ADSK_Масса_Текст=90; ADSK_Наименование=Вертикальный насос TESK типа IN-LINE, DN80, Hmax=22м (3x380V 50Hz IE3); ADSK_Напряжение=400 В; ADSK_Номинальная мощность=11.00 кВт; ADSK_Полная мощность=11.00 кВ·А; B1=260 мм; B2=208 мм; B3=142 мм; B4=124 мм; B5=160 мм; C=66 мм; D=200 мм; D2=160 мм; D3=148 мм; DN=80 мм; F0=200 мм; F1=132 мм; F2=66 мм; F3=125 мм; F4=148 мм; H1=97 мм; H2=263 мм; H3=770 мм; H4=410 мм; L1=450 мм; Напор максимальный=22; Плита_Глубина=204 мм; Плита_Ширина=204 мм
- ТК 80-28/2  7,5kW 3x380V 50Hz IE3: ADSK_Диаметр условный=80 мм; ADSK_Код изделия=55TK8028203380; ADSK_Количество фаз=3; ADSK_Количество фаз числовое=3; ADSK_Марка=ТК 80-28/2  7,5kW 3x380V 50Hz IE3; ADSK_Масса=100; ADSK_Масса_Текст=100; ADSK_Наименование=Вертикальный насос TESK типа IN-LINE, DN80, Hmax=28м (3x380V 50Hz IE3); ADSK_Напряжение=400 В; ADSK_Номинальная мощность=15.00 кВт; ADSK_Полная мощность=15.00 кВ·А; B1=260 мм; B2=208 мм; B3=142 мм; B4=124 мм; B5=160 мм; C=66 мм; D=200 мм; D2=160 мм; D3=148 мм; DN=80 мм; F0=200 мм; F1=132 мм; F2=66 мм; F3=125 мм; F4=148 мм; H1=97 мм; H2=263 мм; H3=770 мм; H4=410 мм; L1=450 мм; Напор максимальный=28; Плита_Глубина=204 мм; Плита_Ширина=204 мм
- ТК 80-30/2  11kW 3x380V 50Hz IE3: ADSK_Диаметр условный=80 мм; ADSK_Код изделия=55TK8030203380; ADSK_Количество фаз=3; ADSK_Количество фаз числовое=3; ADSK_Марка=ТК 80-30/2  11kW 3x380V 50Hz IE3; ADSK_Масса=184; ADSK_Масса_Текст=184; ADSK_Наименование=Вертикальный насос TESK типа IN-LINE, DN80, Hmax=30м (3x380V 50Hz IE3); ADSK_Напряжение=400 В; ADSK_Номинальная мощность=11.00 кВт; ADSK_Полная мощность=11.00 кВ·А; B1=330 мм; B2=255 мм; B3=182 мм; B4=163 мм; B5=144 мм; C=66 мм; D=350 мм; D2=225 мм; D3=226 мм; DN=80 мм; F0=200 мм; F1=132 мм; F2=66 мм; F3=125 мм; F4=148 мм; H1=115 мм; H2=274 мм; H3=931 мм; H4=542 мм; L1=500 мм; Напор максимальный=30; Плита_Глубина=188 мм; Плита_Ширина=188 мм
- ТК 80-38/2  15kW 3x380V 50Hz IE3: ADSK_Диаметр условный=80 мм; ADSK_Код изделия=55TK8038203380; ADSK_Количество фаз=3; ADSK_Количество фаз числовое=3; ADSK_Марка=ТК 80-38/2  15kW 3x380V 50Hz IE3; ADSK_Масса=192; ADSK_Масса_Текст=192; ADSK_Наименование=Вертикальный насос TESK типа IN-LINE, DN80, Hmax=38м (3x380V 50Hz IE3); ADSK_Напряжение=400 В; ADSK_Номинальная мощность=15.00 кВт; ADSK_Полная мощность=15.00 кВ·А; B1=330 мм; B2=255 мм; B3=182 мм; B4=163 мм; B5=144 мм; C=66 мм; D=350 мм; D2=225 мм; D3=226 мм; DN=80 мм; F0=200 мм; F1=132 мм; F2=66 мм; F3=125 мм; F4=148 мм; H1=115 мм; H2=274 мм; H3=964 мм; H4=575 мм; L1=500 мм; Напор максимальный=38; Плита_Глубина=188 мм; Плита_Ширина=188 мм
- ТК 80-47/2  18,5kW 3x380V 50Hz IE3: ADSK_Диаметр условный=80 мм; ADSK_Код изделия=55TK8047203380; ADSK_Количество фаз=3; ADSK_Количество фаз числовое=3; ADSK_Марка=ТК 80-47/2  18,5kW 3x380V 50Hz IE3; ADSK_Масса=208; ADSK_Масса_Текст=208; ADSK_Наименование=Вертикальный насос TESK типа IN-LINE, DN80, Hmax=47м (3x380V 50Hz IE3); ADSK_Напряжение=400 В; ADSK_Номинальная мощность=18.50 кВт; ADSK_Полная мощность=18.50 кВ·А; B1=330 мм; B2=255 мм; B3=182 мм; B4=163 мм; B5=144 мм; C=66 мм; D=350 мм; D2=225 мм; D3=226 мм; DN=80 мм; F0=200 мм; F1=132 мм; F2=66 мм; F3=125 мм; F4=148 мм; H1=115 мм; H2=274 мм; H3=964 мм; H4=575 мм; L1=500 мм; Напор максимальный=47; Плита_Глубина=188 мм; Плита_Ширина=188 мм
- ТК 80-54/2  22kW 3x380V 50Hz IE3: ADSK_Диаметр условный=80 мм; ADSK_Код изделия=55TK8054203380; ADSK_Количество фаз=3; ADSK_Количество фаз числовое=3; ADSK_Марка=ТК 80-54/2  22kW 3x380V 50Hz IE3; ADSK_Масса=244; ADSK_Масса_Текст=244; ADSK_Наименование=Вертикальный насос TESK типа IN-LINE, DN80, Hmax=54м (3x380V 50Hz IE3); ADSK_Напряжение=400 В; ADSK_Номинальная мощность=22.00 кВт; ADSK_Полная мощность=22.00 кВ·А; B1=330 мм; B2=280 мм; B3=182 мм; B4=163 мм; B5=144 мм; C=66 мм; D=350 мм; D2=250 мм; D3=226 мм; DN=80 мм; F0=200 мм; F1=132 мм; F2=66 мм; F3=125 мм; F4=148 мм; H1=115 мм; H2=274 мм; H3=994 мм; H4=605 мм; L1=500 мм; Напор максимальный=54; Плита_Глубина=188 мм; Плита_Ширина=188 мм
- ТК 80-67/2  30kW 3x380V 50Hz IE3: ADSK_Диаметр условный=80 мм; ADSK_Код изделия=55TK8067203380; ADSK_Количество фаз=3; ADSK_Количество фаз числовое=3; ADSK_Марка=ТК 80-67/2  30kW 3x380V 50Hz IE3; ADSK_Масса=302; ADSK_Масса_Текст=302; ADSK_Наименование=Вертикальный насос TESK типа IN-LINE, DN80, Hmax=67м (3x380V 50Hz IE3); ADSK_Напряжение=400 В; ADSK_Номинальная мощность=30.00 кВт; ADSK_Полная мощность=30.00 кВ·А; B1=400 мм; B2=305 мм; B3=182 мм; B4=163 мм; B5=144 мм; C=66 мм; D=400 мм; D2=275 мм; D3=226 мм; DN=80 мм; F0=200 мм; F1=132 мм; F2=66 мм; F3=125 мм; F4=148 мм; H1=115 мм; H2=274 мм; H3=1054 мм; H4=665 мм; L1=500 мм; Напор максимальный=67; Плита_Глубина=188 мм; Плита_Ширина=188 мм
- ТК 100-9/2 2,2kW 3x380V 50Hz IE3: ADSK_Диаметр условный=100 мм; ADSK_Код изделия=55TK1009203380; ADSK_Количество фаз=3; ADSK_Количество фаз числовое=3; ADSK_Марка=ТК 100-9/2  2,2kW 3x380V 50Hz IE3; ADSK_Масса=54; ADSK_Масса_Текст=54; ADSK_Наименование=Вертикальный насос TESK типа IN-LINE, DN100, Hmax=9м (3x380V 50Hz IE3); ADSK_Напряжение=400 В; ADSK_Номинальная мощность=2.20 кВт; ADSK_Полная мощность=2.20 кВ·А; B1=175 мм; B2=155 мм; B3=134 мм; B4=101 мм; B5=160 мм; C=78 мм; D=140 мм; D2=100 мм; D3=102 мм; DN=100 мм; F0=220 мм; F1=156 мм; F2=78 мм; F3=138 мм; F4=163 мм; H1=105 мм; H2=211 мм; H3=609 мм; H4=293 мм; L1=450 мм; Напор максимальный=9; Плита_Глубина=204 мм; Плита_Ширина=204 мм
- ТК 100-9/2  2,2kW 1x220V 50Hz IE3: ADSK_Диаметр условный=100 мм; ADSK_Код изделия=55TK1009201220; ADSK_Количество фаз=1; ADSK_Количество фаз числовое=1; ADSK_Марка=ТК 100-9/2  2,2kW 1x220V 50Hz IE3; ADSK_Масса=54; ADSK_Масса_Текст=54; ADSK_Наименование=Вертикальный насос TESK типа IN-LINE, DN100, Hmax=9м (1x220V 50Hz IE3); ADSK_Напряжение=230 В; ADSK_Номинальная мощность=2.20 кВт; ADSK_Полная мощность=2.20 кВ·А; B1=175 мм; B2=155 мм; B3=134 мм; B4=101 мм; B5=160 мм; C=78 мм; D=140 мм; D2=100 мм; D3=102 мм; DN=100 мм; F0=220 мм; F1=156 мм; F2=78 мм; F3=138 мм; F4=163 мм; H1=105 мм; H2=211 мм; H3=609 мм; H4=293 мм; L1=450 мм; Напор максимальный=9; Плита_Глубина=204 мм; Плита_Ширина=204 мм
- ТК 100-15/2  4kW 3x380V 50Hz IE3: ADSK_Диаметр условный=100 мм; ADSK_Код изделия=55TK10015203380; ADSK_Количество фаз=3; ADSK_Количество фаз числовое=3; ADSK_Марка=ТК 100-15/2  4kW 3x380V 50Hz IE3; ADSK_Масса=70; ADSK_Масса_Текст=70; ADSK_Наименование=Вертикальный насос TESK типа IN-LINE, DN100, Hmax=15м (3x380V 50Hz IE3); ADSK_Напряжение=400 В; ADSK_Номинальная мощность=4.00 кВт; ADSK_Полная мощность=4.00 кВ·А; B1=215 мм; B2=190 мм; B3=134 мм; B4=101 мм; B5=160 мм; C=78 мм; D=160 мм; D2=120 мм; D3=102 мм; DN=100 мм; F0=220 мм; F1=156 мм; F2=78 мм; F3=138 мм; F4=163 мм; H1=105 мм; H2=212 мм; H3=652 мм; H4=335 мм; L1=450 мм; Напор максимальный=15; Плита_Глубина=204 мм; Плита_Ширина=204 мм
- ТК 100-17/2  5,5kW 3x380V 50Hz IE3: ADSK_Диаметр условный=100 мм; ADSK_Код изделия=55TK10017203380; ADSK_Количество фаз=3; ADSK_Количество фаз числовое=3; ADSK_Марка=ТК 100-17/2  5,5kW 3x380V 50Hz IE3; ADSK_Масса=98; ADSK_Масса_Текст=98; ADSK_Наименование=Вертикальный насос TESK типа IN-LINE, DN100, Hmax=17м (3x380V 50Hz IE3); ADSK_Напряжение=400 В; ADSK_Номинальная мощность=5.50 кВт; ADSK_Полная мощность=5.50 кВ·А; B1=260 мм; B2=205 мм; B3=150 мм; B4=117 мм; B5=144 мм; C=78 мм; D=200 мм; D2=160 мм; D3=134 мм; DN=100 мм; F0=220 мм; F1=156 мм; F2=78 мм; F3=138 мм; F4=163 мм; H1=140 мм; H2=237 мм; H3=787 мм; H4=410 мм; L1=500 мм; Напор максимальный=17; Плита_Глубина=188 мм; Плита_Ширина=188 мм
- ТК 100-22/2  7,5kW 3x380V 50Hz IE3: ADSK_Диаметр условный=100 мм; ADSK_Код изделия=55TK10022203380; ADSK_Количество фаз=3; ADSK_Количество фаз числовое=3; ADSK_Марка=ТК 100-22/2  7,5kW 3x380V 50Hz IE3; ADSK_Масса=106; ADSK_Масса_Текст=106; ADSK_Наименование=Вертикальный насос TESK типа IN-LINE, DN100, Hmax=22м (3x380V 50Hz IE3); ADSK_Напряжение=400 В; ADSK_Номинальная мощность=7.50 кВт; ADSK_Полная мощность=7.50 кВ·А; B1=260 мм; B2=205 мм; B3=150 мм; B4=117 мм; B5=144 мм; C=78 мм; D=200 мм; D2=160 мм; D3=134 мм; DN=100 мм; F0=220 мм; F1=156 мм; F2=78 мм; F3=138 мм; F4=163 мм; H1=140 мм; H2=237 мм; H3=787 мм; H4=410 мм; L1=500 мм; Напор максимальный=22; Плита_Глубина=188 мм; Плита_Ширина=188 мм
- ТК 100-27/2  11kW 3x380V 50Hz IE3: ADSK_Диаметр условный=100 мм; ADSK_Код изделия=55TK10027203380; ADSK_Количество фаз=3; ADSK_Количество фаз числовое=3; ADSK_Марка=ТК 100-27/2  11kW 3x380V 50Hz IE3; ADSK_Масса=184; ADSK_Масса_Текст=184; ADSK_Наименование=Вертикальный насос TESK типа IN-LINE, DN100, Hmax=27м (3x380V 50Hz IE3); ADSK_Напряжение=400 В; ADSK_Номинальная мощность=11.00 кВт; ADSK_Полная мощность=11.00 кВ·А; B1=350 мм; B2=255 мм; B3=147 мм; B4=123 мм; B5=144 мм; C=78 мм; D=350 мм; D2=225 мм; D3=146 мм; DN=100 мм; F0=220 мм; F1=156 мм; F2=78 мм; F3=138 мм; F4=163 мм; H1=140 мм; H2=252 мм; H3=934 мм; H4=542 мм; L1=550 мм; Напор максимальный=27; Плита_Глубина=188 мм; Плита_Ширина=188 мм
- ТК 100-33/2  15kW 3x380V 50Hz IE3: ADSK_Диаметр условный=100 мм; ADSK_Код изделия=55TK10033203380; ADSK_Количество фаз=3; ADSK_Количество фаз числовое=3; ADSK_Марка=ТК 100-33/2  15kW 3x380V 50Hz IE3; ADSK_Масса=194; ADSK_Масса_Текст=194; ADSK_Наименование=Вертикальный насос TESK типа IN-LINE, DN100, Hmax=33м (3x380V 50Hz IE3); ADSK_Напряжение=400 В; ADSK_Номинальная мощность=15.00 кВт; ADSK_Полная мощность=15.00 кВ·А; B1=350 мм; B2=255 мм; B3=147 мм; B4=123 мм; B5=144 мм; C=78 мм; D=350 мм; D2=225 мм; D3=146 мм; DN=100 мм; F0=220 мм; F1=156 мм; F2=78 мм; F3=138 мм; F4=163 мм; H1=140 мм; H2=252 мм; H3=967 мм; H4=575 мм; L1=550 мм; Напор максимальный=33; Плита_Глубина=188 мм; Плита_Ширина=188 мм
- ТК 100-40/2  18,5kW 3x380V 50Hz IE3: ADSK_Диаметр условный=100 мм; ADSK_Код изделия=55TK10040203380; ADSK_Количество фаз=3; ADSK_Количество фаз числовое=3; ADSK_Марка=ТК 100-40/2  18,5kW 3x380V 50Hz IE3; ADSK_Масса=216; ADSK_Масса_Текст=216; ADSK_Наименование=Вертикальный насос TESK типа IN-LINE, DN100, Hmax=40м (3x380V 50Hz IE3); ADSK_Напряжение=400 В; ADSK_Номинальная мощность=18.50 кВт; ADSK_Полная мощность=18.50 кВ·А; B1=350 мм; B2=255 мм; B3=181 мм; B4=152 мм; B5=230 мм; C=78 мм; D=350 мм; D2=225 мм; D3=204 мм; DN=100 мм; F0=220 мм; F1=156 мм; F2=78 мм; F3=138 мм; F4=163 мм; H1=140 мм; H2=266 мм; H3=981 мм; H4=575 мм; L1=550 мм; Напор максимальный=40; Плита_Глубина=274 мм; Плита_Ширина=274 мм
- ТК 100-48/2  22kW 3x380V 50Hz IE3: ADSK_Диаметр условный=100 мм; ADSK_Код изделия=55TK10048203380; ADSK_Количество фаз=3; ADSK_Количество фаз числовое=3; ADSK_Марка=ТК 100-48/2  22kW 3x380V 50Hz IE3; ADSK_Масса=258; ADSK_Масса_Текст=258; ADSK_Наименование=Вертикальный насос TESK типа IN-LINE, DN100, Hmax=48м (3x380V 50Hz IE3); ADSK_Напряжение=400 В; ADSK_Номинальная мощность=22.00 кВт; ADSK_Полная мощность=22.00 кВ·А; B1=350 мм; B2=280 мм; B3=181 мм; B4=152 мм; B5=230 мм; C=78 мм; D=350 мм; D2=250 мм; D3=204 мм; DN=100 мм; F0=220 мм; F1=156 мм; F2=78 мм; F3=138 мм; F4=163 мм; H1=140 мм; H2=266 мм; H3=1011 мм; H4=605 мм; L1=550 мм; Напор максимальный=48; Плита_Глубина=274 мм; Плита_Ширина=274 мм
- ТК 100-52/2  30kW 3x380V 50Hz IE3: ADSK_Диаметр условный=100 мм; ADSK_Код изделия=55TK10052203380; ADSK_Количество фаз=3; ADSK_Количество фаз числовое=3; ADSK_Марка=ТК 100-52/2  30kW 3x380V 50Hz IE3; ADSK_Масса=312; ADSK_Масса_Текст=312; ADSK_Наименование=Вертикальный насос TESK типа IN-LINE, DN100, Hmax=52м (3x380V 50Hz IE3); ADSK_Напряжение=400 В; ADSK_Номинальная мощность=30.00 кВт; ADSK_Полная мощность=30.00 кВ·А; B1=400 мм; B2=305 мм; B3=181 мм; B4=152 мм; B5=230 мм; C=78 мм; D=400 мм; D2=275 мм; D3=204 мм; DN=100 мм; F0=220 мм; F1=156 мм; F2=78 мм; F3=138 мм; F4=163 мм; H1=140 мм; H2=266 мм; H3=1071 мм; H4=665 мм; L1=550 мм; Напор максимальный=52; Плита_Глубина=274 мм; Плита_Ширина=274 мм
- ТК 125-11/4  5,5kW 3x380V 50Hz IE3: ADSK_Диаметр условный=125 мм; ADSK_Код изделия=55TK12511403380; ADSK_Количество фаз=3; ADSK_Количество фаз числовое=3; ADSK_Марка=ТК 125-11/4  5,5kW 3x380V 50Hz IE3; ADSK_Масса=142; ADSK_Масса_Текст=142; ADSK_Наименование=Вертикальный насос TESK типа IN-LINE, DN125, Hmax=11м (3x380V 50Hz IE3); ADSK_Напряжение=400 В; ADSK_Номинальная мощность=5.50 кВт; ADSK_Полная мощность=5.50 кВ·А; B1=260 мм; B2=208 мм; B3=216 мм; B4=176 мм; B5=230 мм; C=92 мм; D=200 мм; D2=160 мм; D3=252 мм; DN=125 мм; F0=250 мм; F1=184 мм; F2=92 мм; F3=156 мм; F4=185 мм; H1=215 мм; H2=256 мм; H3=853 мм; H4=382 мм; L1=620 мм; Напор максимальный=11; Плита_Глубина=274 мм; Плита_Ширина=274 мм
- ТК 125-14/4  7,5kW 3x380V 50Hz IE3: ADSK_Диаметр условный=125 мм; ADSK_Код изделия=55TK12514403380; ADSK_Количество фаз=3; ADSK_Количество фаз числовое=3; ADSK_Марка=ТК 125-14/4  7,5kW 3x380V 50Hz IE3; ADSK_Масса=152; ADSK_Масса_Текст=152; ADSK_Наименование=Вертикальный насос TESK типа IN-LINE, DN125, Hmax=14м (3x380V 50Hz IE3); ADSK_Напряжение=400 В; ADSK_Номинальная мощность=7.50 кВт; ADSK_Полная мощность=7.50 кВ·А; B1=260 мм; B2=208 мм; B3=216 мм; B4=176 мм; B5=230 мм; C=92 мм; D=200 мм; D2=160 мм; D3=252 мм; DN=125 мм; F0=250 мм; F1=184 мм; F2=92 мм; F3=156 мм; F4=185 мм; H1=215 мм; H2=256 мм; H3=853 мм; H4=382 мм; L1=620 мм; Напор максимальный=14; Плита_Глубина=274 мм; Плита_Ширина=274 мм
- ТК 125-18/4  11kW 3x380V 50Hz IE3: ADSK_Диаметр условный=125 мм; ADSK_Код изделия=55TK12518403380; ADSK_Количество фаз=3; ADSK_Количество фаз числовое=3; ADSK_Марка=ТК 125-18/4  11kW 3x380V 50Hz IE3; ADSK_Масса=258; ADSK_Масса_Текст=258; ADSK_Наименование=Вертикальный насос TESK типа IN-LINE, DN125, Hmax=18м (3x380V 50Hz IE3); ADSK_Напряжение=400 В; ADSK_Номинальная мощность=11.00 кВт; ADSK_Полная мощность=11.00 кВ·А; B1=330 мм; B2=255 мм; B3=211 мм; B4=177 мм; B5=230 мм; C=92 мм; D=350 мм; D2=225 мм; D3=254 мм; DN=125 мм; F0=250 мм; F1=184 мм; F2=92 мм; F3=156 мм; F4=185 мм; H1=215 мм; H2=297 мм; H3=1016 мм; H4=504 мм; L1=800 мм; Напор максимальный=18; Плита_Глубина=274 мм; Плита_Ширина=274 мм
- ТК 125-22/4  15kW 3x380V 50Hz IE3: ADSK_Диаметр условный=125 мм; ADSK_Код изделия=55TK12522403380; ADSK_Количество фаз=3; ADSK_Количество фаз числовое=3; ADSK_Марка=ТК 125-22/4  15kW 3x380V 50Hz IE3; ADSK_Масса=310; ADSK_Масса_Текст=310; ADSK_Наименование=Вертикальный насос TESK типа IN-LINE, DN125, Hmax=22м (3x380V 50Hz IE3); ADSK_Напряжение=400 В; ADSK_Номинальная мощность=15.00 кВт; ADSK_Полная мощность=15.00 кВ·А; B1=330 мм; B2=255 мм; B3=236 мм; B4=208 мм; B5=230 мм; C=92 мм; D=350 мм; D2=225 мм; D3=316 мм; DN=125 мм; F0=250 мм; F1=184 мм; F2=92 мм; F3=156 мм; F4=185 мм; H1=215 мм; H2=297 мм; H3=1035 мм; H4=523 мм; L1=800 мм; Напор максимальный=22; Плита_Глубина=274 мм; Плита_Ширина=274 мм
- ТК 125-28/4  18,5kW 3x380V 50Hz IE3: ADSK_Диаметр условный=125 мм; ADSK_Код изделия=55TK12528403380; ADSK_Количество фаз=3; ADSK_Количество фаз числовое=3; ADSK_Марка=ТК 125-28/4  18,5kW 3x380V 50Hz IE3; ADSK_Масса=350; ADSK_Масса_Текст=350; ADSK_Наименование=Вертикальный насос TESK типа IN-LINE, DN125, Hmax=28м (3x380V 50Hz IE3); ADSK_Напряжение=400 В; ADSK_Номинальная мощность=18.50 кВт; ADSK_Полная мощность=18.50 кВ·А; B1=330 мм; B2=280 мм; B3=236 мм; B4=208 мм; B5=230 мм; C=92 мм; D=350 мм; D2=250 мм; D3=316 мм; DN=125 мм; F0=250 мм; F1=184 мм; F2=92 мм; F3=156 мм; F4=185 мм; H1=215 мм; H2=316 мм; H3=1079 мм; H4=548 мм; L1=800 мм; Напор максимальный=28; Плита_Глубина=274 мм; Плита_Ширина=274 мм
- ТК 125-32/4  22kW 3x380V 50Hz IE3: ADSK_Диаметр условный=125 мм; ADSK_Код изделия=55TK12532403380; ADSK_Количество фаз=3; ADSK_Количество фаз числовое=3; ADSK_Марка=ТК 125-32/4  22kW 3x380V 50Hz IE3; ADSK_Масса=376; ADSK_Масса_Текст=376; ADSK_Наименование=Вертикальный насос TESK типа IN-LINE, DN125, Hmax=32м (3x380V 50Hz IE3); ADSK_Напряжение=400 В; ADSK_Номинальная мощность=22.00 кВт; ADSK_Полная мощность=22.00 кВ·А; B1=330 мм; B2=280 мм; B3=236 мм; B4=208 мм; B5=230 мм; C=92 мм; D=350 мм; D2=250 мм; D3=316 мм; DN=125 мм; F0=250 мм; F1=184 мм; F2=92 мм; F3=156 мм; F4=185 мм; H1=215 мм; H2=316 мм; H3=1111 мм; H4=580 мм; L1=800 мм; Напор максимальный=32; Плита_Глубина=274 мм; Плита_Ширина=274 мм
- ТК 125-40/4  30kW 3x380V 50Hz IE3: ADSK_Диаметр условный=125 мм; ADSK_Код изделия=55TK12540403380; ADSK_Количество фаз=3; ADSK_Количество фаз числовое=3; ADSK_Марка=ТК 125-40/4  30kW 3x380V 50Hz IE3; ADSK_Масса=462; ADSK_Масса_Текст=462; ADSK_Наименование=Вертикальный насос TESK типа IN-LINE, DN125, Hmax=40м (3x380V 50Hz IE3); ADSK_Напряжение=400 В; ADSK_Номинальная мощность=30.00 кВт; ADSK_Полная мощность=30.00 кВ·А; B1=400 мм; B2=305 мм; B3=272 мм; B4=248 мм; B5=230 мм; C=92 мм; D=400 мм; D2=275 мм; D3=396 мм; DN=125 мм; F0=250 мм; F1=184 мм; F2=92 мм; F3=156 мм; F4=185 мм; H1=215 мм; H2=323 мм; H3=1188 мм; H4=650 мм; L1=800 мм; Напор максимальный=40; Плита_Глубина=274 мм; Плита_Ширина=274 мм
- ТК 125-48/4  37kW 3x380V 50Hz IE3: ADSK_Диаметр условный=125 мм; ADSK_Код изделия=55TK12548403380; ADSK_Количество фаз=3; ADSK_Количество фаз числовое=3; ADSK_Марка=ТК 125-48/4  37kW 3x380V 50Hz IE3; ADSK_Масса=518; ADSK_Масса_Текст=518; ADSK_Наименование=Вертикальный насос TESK типа IN-LINE, DN125, Hmax=48м (3x380V 50Hz IE3); ADSK_Напряжение=400 В; ADSK_Номинальная мощность=37.00 кВт; ADSK_Полная мощность=37.00 кВ·А; B1=450 мм; B2=335 мм; B3=272 мм; B4=248 мм; B5=230 мм; C=92 мм; D=450 мм; D2=305 мм; D3=396 мм; DN=125 мм; F0=250 мм; F1=184 мм; F2=92 мм; F3=156 мм; F4=185 мм; H1=215 мм; H2=323 мм; H3=1233 мм; H4=695 мм; L1=800 мм; Напор максимальный=48; Плита_Глубина=274 мм; Плита_Ширина=274 мм
- ТК 150-12,5/4  11kW 3x380V 50Hz IE3: ADSK_Диаметр условный=150 мм; ADSK_Код изделия=55TK150125403380; ADSK_Количество фаз=3; ADSK_Количество фаз числовое=3; ADSK_Марка=ТК 150-12,5/4  11kW 3x380V 50Hz IE3; ADSK_Масса=260; ADSK_Масса_Текст=260; ADSK_Наименование=Вертикальный насос TESK типа IN-LINE, DN150, Hmax=12.5м (3x380V 50Hz IE3); ADSK_Напряжение=400 В; ADSK_Номинальная мощность=11.00 кВт; ADSK_Полная мощность=11.00 кВ·А; B1=315 мм; B2=255 мм; B3=217 мм; B4=180 мм; B5=230 мм; C=106 мм; D=350 мм; D2=225 мм; D3=260 мм; DN=150 мм; F0=285 мм; F1=212 мм; F2=106 мм; F3=178 мм; F4=211 мм; H1=215 мм; H2=293 мм; H3=1050 мм; H4=542 мм; L1=800 мм; Напор максимальный=12.5; Плита_Глубина=274 мм; Плита_Ширина=274 мм
- ТК 150-17/4  15kW 3x380V 50Hz IE3: ADSK_Диаметр условный=150 мм; ADSK_Код изделия=55TK15017403380; ADSK_Количество фаз=3; ADSK_Количество фаз числовое=3; ADSK_Марка=ТК 150-17/4  15kW 3x380V 50Hz IE3; ADSK_Масса=276; ADSK_Масса_Текст=276; ADSK_Наименование=Вертикальный насос TESK типа IN-LINE, DN150, Hmax=17м (3x380V 50Hz IE3); ADSK_Напряжение=400 В; ADSK_Номинальная мощность=15.00 кВт; ADSK_Полная мощность=15.00 кВ·А; B1=315 мм; B2=255 мм; B3=217 мм; B4=180 мм; B5=230 мм; C=106 мм; D=350 мм; D2=225 мм; D3=260 мм; DN=150 мм; F0=285 мм; F1=212 мм; F2=106 мм; F3=178 мм; F4=211 мм; H1=215 мм; H2=293 мм; H3=1083 мм; H4=575 мм; L1=800 мм; Напор максимальный=17; Плита_Глубина=274 мм; Плита_Ширина=274 мм
- ТК 150-21/4  18,5kW 3x380V 50Hz IE3: ADSK_Диаметр условный=150 мм; ADSK_Код изделия=55TK15021403380; ADSK_Количество фаз=3; ADSK_Количество фаз числовое=3; ADSK_Марка=ТК 150-21/4  18,5kW 3x380V 50Hz IE3; ADSK_Масса=314; ADSK_Масса_Текст=314; ADSK_Наименование=Вертикальный насос TESK типа IN-LINE, DN150, Hmax=21м (3x380V 50Hz IE3); ADSK_Напряжение=400 В; ADSK_Номинальная мощность=18.50 кВт; ADSK_Полная мощность=18.50 кВ·А; B1=360 мм; B2=280 мм; B3=217 мм; B4=180 мм; B5=230 мм; C=106 мм; D=350 мм; D2=250 мм; D3=260 мм; DN=150 мм; F0=285 мм; F1=212 мм; F2=106 мм; F3=178 мм; F4=211 мм; H1=215 мм; H2=293 мм; H3=1083 мм; H4=575 мм; L1=800 мм; Напор максимальный=21; Плита_Глубина=274 мм; Плита_Ширина=274 мм
- ТК 150-25/4  22kW 3x380V 50Hz IE3: ADSK_Диаметр условный=150 мм; ADSK_Код изделия=55TK15025403380; ADSK_Количество фаз=3; ADSK_Количество фаз числовое=3; ADSK_Марка=ТК 150-25/4  22kW 3x380V 50Hz IE3; ADSK_Масса=372; ADSK_Масса_Текст=372; ADSK_Наименование=Вертикальный насос TESK типа IN-LINE, DN150, Hmax=25м (3x380V 50Hz IE3); ADSK_Напряжение=400 В; ADSK_Номинальная мощность=22.00 кВт; ADSK_Полная мощность=22.00 кВ·А; B1=360 мм; B2=280 мм; B3=238 мм; B4=208 мм; B5=230 мм; C=106 мм; D=350 мм; D2=250 мм; D3=316 мм; DN=150 мм; F0=285 мм; F1=212 мм; F2=106 мм; F3=178 мм; F4=211 мм; H1=215 мм; H2=293 мм; H3=1113 мм; H4=605 мм; L1=800 мм; Напор максимальный=25; Плита_Глубина=274 мм; Плита_Ширина=274 мм
- ТК 150-33/4  30kW 3x380V 50Hz IE3: ADSK_Диаметр условный=150 мм; ADSK_Код изделия=55TK15033403380; ADSK_Количество фаз=3; ADSK_Количество фаз числовое=3; ADSK_Марка=ТК 150-33/4  30kW 3x380V 50Hz IE3; ADSK_Масса=430; ADSK_Масса_Текст=430; ADSK_Наименование=Вертикальный насос TESK типа IN-LINE, DN150, Hmax=33м (3x380V 50Hz IE3); ADSK_Напряжение=400 В; ADSK_Номинальная мощность=30.00 кВт; ADSK_Полная мощность=30.00 кВ·А; B1=400 мм; B2=305 мм; B3=238 мм; B4=208 мм; B5=230 мм; C=106 мм; D=400 мм; D2=275 мм; D3=316 мм; DN=150 мм; F0=285 мм; F1=212 мм; F2=106 мм; F3=178 мм; F4=211 мм; H1=215 мм; H2=293 мм; H3=1208 мм; H4=700 мм; L1=800 мм; Напор максимальный=33; Плита_Глубина=274 мм; Плита_Ширина=274 мм
- ТК 150-40/4  37kW 3x380V 50Hz IE3: ADSK_Диаметр условный=150 мм; ADSK_Код изделия=55TK15040403380; ADSK_Количество фаз=3; ADSK_Количество фаз числовое=3; ADSK_Марка=ТК 150-40/4  37kW 3x380V 50Hz IE3; ADSK_Масса=532; ADSK_Масса_Текст=532; ADSK_Наименование=Вертикальный насос TESK типа IN-LINE, DN150, Hmax=40м (3x380V 50Hz IE3); ADSK_Напряжение=400 В; ADSK_Номинальная мощность=37.00 кВт; ADSK_Полная мощность=37.00 кВ·А; B1=450 мм; B2=335 мм; B3=267 мм; B4=248 мм; B5=230 мм; C=106 мм; D=450 мм; D2=305 мм; D3=396 мм; DN=150 мм; F0=285 мм; F1=212 мм; F2=106 мм; F3=178 мм; F4=211 мм; H1=230 мм; H2=323 мм; H3=1258 мм; H4=705 мм; L1=900 мм; Напор максимальный=40; Плита_Глубина=274 мм; Плита_Ширина=274 мм
- ТК 150-50/4  45kW 3x380V 50Hz IE3: ADSK_Диаметр условный=150 мм; ADSK_Код изделия=55TK15050403380; ADSK_Количество фаз=3; ADSK_Количество фаз числовое=3; ADSK_Марка=ТК 150-50/4  45kW 3x380V 50Hz IE3; ADSK_Масса=556; ADSK_Масса_Текст=556; ADSK_Наименование=Вертикальный насос TESK типа IN-LINE, DN150, Hmax=50м (3x380V 50Hz IE3); ADSK_Напряжение=400 В; ADSK_Номинальная мощность=45.00 кВт; ADSK_Полная мощность=45.00 кВ·А; B1=450 мм; B2=335 мм; B3=267 мм; B4=248 мм; B5=230 мм; C=106 мм; D=450 мм; D2=305 мм; D3=396 мм; DN=150 мм; F0=285 мм; F1=212 мм; F2=106 мм; F3=178 мм; F4=211 мм; H1=230 мм; H2=323 мм; H3=1283 мм; H4=730 мм; L1=900 мм; Напор максимальный=50; Плита_Глубина=274 мм; Плита_Ширина=274 мм
